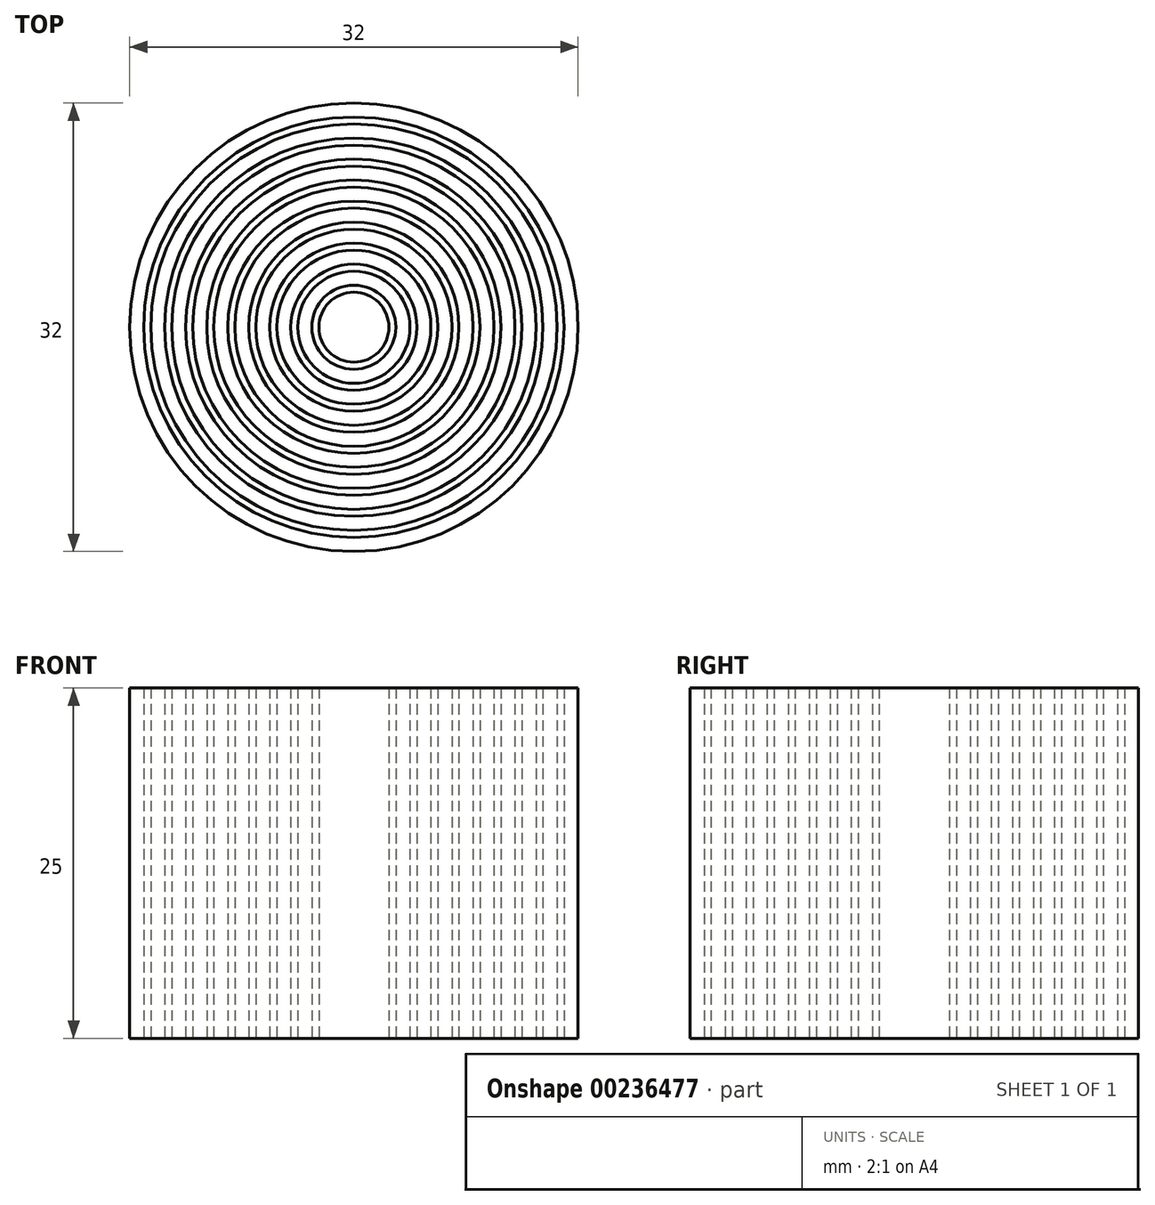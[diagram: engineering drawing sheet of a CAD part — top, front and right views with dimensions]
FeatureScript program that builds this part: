
annotation { "Feature Type Name" : "Feature", "Feature Type Description" : "" }
export const myFeature = defineFeature(function(context is Context, id is Id, definition is map)
    precondition{}
    {
        {
            var Q0;
            Q0=qCreatedBy(makeId("Top.planeOp"),FACE);
            var sketch = newSketch(context, id + "F0", { "sketchPlane" : qUnion([Q0])});
            skCircle(sketch, "E0", {"center": v(0, 0) * mm, "radius": 2.5 * mm});
            skCircle(sketch, "E1", {"center": v(0, 0) * mm, "radius": 3 * mm});
            skCircle(sketch, "E2", {"center": v(0, 0) * mm, "radius": 4 * mm});
            skCircle(sketch, "E3", {"center": v(0, 0) * mm, "radius": 4.5 * mm});
            skCircle(sketch, "E4", {"center": v(0, 0) * mm, "radius": 5.5 * mm});
            skCircle(sketch, "E5", {"center": v(0, 0) * mm, "radius": 6 * mm});
            skCircle(sketch, "E6", {"center": v(0, 0) * mm, "radius": 7 * mm});
            skCircle(sketch, "E7", {"center": v(0, 0) * mm, "radius": 7.5 * mm});
            skCircle(sketch, "E8", {"center": v(0, 0) * mm, "radius": 8.5 * mm});
            skCircle(sketch, "E9", {"center": v(0, 0) * mm, "radius": 9 * mm});
            skCircle(sketch, "E10", {"center": v(0, 0) * mm, "radius": 10 * mm});
            skCircle(sketch, "E11", {"center": v(0, 0) * mm, "radius": 10.5 * mm});
            skCircle(sketch, "E12", {"center": v(0, 0) * mm, "radius": 11.5 * mm});
            skCircle(sketch, "E13", {"center": v(0, 0) * mm, "radius": 12 * mm});
            skCircle(sketch, "E14", {"center": v(0, 0) * mm, "radius": 13 * mm});
            skCircle(sketch, "E15", {"center": v(0, 0) * mm, "radius": 13.5 * mm});
            skCircle(sketch, "E16", {"center": v(0, 0) * mm, "radius": 14.5 * mm});
            skCircle(sketch, "E17", {"center": v(0, 0) * mm, "radius": 15 * mm});
            skCircle(sketch, "E18", {"center": v(0, 0) * mm, "radius": 16 * mm});
            skSolve(sketch);
        }
        {
            var Q0;
            Q0=makeQuery(id+"F0.imprint","IMPRINT",FACE,{"disambiguationData":[TD([[makeQuery(id+"F0.imprint","IMPRINT",EDGE,{"derivedFrom":sQuery(id+"F0.wireOp",EDGE,"E0")}),1.0]])]});
            var Q1;
            Q1=makeQuery(id+"F0.imprint","IMPRINT",FACE,{"disambiguationData":[TD([[makeQuery(id+"F0.imprint","IMPRINT",EDGE,{"derivedFrom":sQuery(id+"F0.wireOp",EDGE,"E1")}),-1.0]])]});
            var Q2;
            Q2=makeQuery(id+"F0.imprint","IMPRINT",FACE,{"disambiguationData":[TD([[makeQuery(id+"F0.imprint","IMPRINT",EDGE,{"derivedFrom":sQuery(id+"F0.wireOp",EDGE,"E3")}),-1.0]])]});
            var Q3;
            Q3=makeQuery(id+"F0.imprint","IMPRINT",FACE,{"disambiguationData":[TD([[makeQuery(id+"F0.imprint","IMPRINT",EDGE,{"derivedFrom":sQuery(id+"F0.wireOp",EDGE,"E5")}),-1.0]])]});
            var Q4;
            Q4=makeQuery(id+"F0.imprint","IMPRINT",FACE,{"disambiguationData":[TD([[makeQuery(id+"F0.imprint","IMPRINT",EDGE,{"derivedFrom":sQuery(id+"F0.wireOp",EDGE,"E7")}),-1.0]])]});
            var Q5;
            Q5=makeQuery(id+"F0.imprint","IMPRINT",FACE,{"disambiguationData":[TD([[makeQuery(id+"F0.imprint","IMPRINT",EDGE,{"derivedFrom":sQuery(id+"F0.wireOp",EDGE,"E9")}),-1.0]])]});
            var Q6;
            Q6=makeQuery(id+"F0.imprint","IMPRINT",FACE,{"disambiguationData":[TD([[makeQuery(id+"F0.imprint","IMPRINT",EDGE,{"derivedFrom":sQuery(id+"F0.wireOp",EDGE,"E11")}),-1.0]])]});
            var Q7;
            Q7=makeQuery(id+"F0.imprint","IMPRINT",FACE,{"disambiguationData":[TD([[makeQuery(id+"F0.imprint","IMPRINT",EDGE,{"derivedFrom":sQuery(id+"F0.wireOp",EDGE,"E13")}),-1.0]])]});
            var Q8;
            Q8=makeQuery(id+"F0.imprint","IMPRINT",FACE,{"disambiguationData":[TD([[makeQuery(id+"F0.imprint","IMPRINT",EDGE,{"derivedFrom":sQuery(id+"F0.wireOp",EDGE,"E15")}),-1.0]])]});
            var Q9;
            Q9=makeQuery(id+"F0.imprint","IMPRINT",FACE,{"disambiguationData":[TD([[makeQuery(id+"F0.imprint","IMPRINT",EDGE,{"derivedFrom":sQuery(id+"F0.wireOp",EDGE,"E17")}),-1.0]])]});
            extrude(context, id + "F1", {"entities" : qUnion([Q0, Q1, Q2, Q3, Q4, Q5, Q6, Q7, Q8, Q9]), "depth" : 25 * mm, "offsetDistance" : 25 * mm});
        }
    });
